# Revit family: Roof Decking-Side
name_source: partatom
category: Detail Items
revit_build: Autodesk Revit Architecture 2012 (Build: 20110210_1515)
units: mm (PartAtom-declared; Revit-internal decimal feet)

## types (26) — shared parameters

## per-type parameters (varying)
| type | Gauge | Height | Keynote | Rib Max | Rib Min | Width |
| 1 IR 20 | 20 | 0' - 1" | 05 31 00.C1 | 0' - 3" | 0' - 1" | 0' - 4" |
| 4.5 LS 16 | 16 | 0' - 4 1/2" | 05 31 00.C18 | 0' - 8" | 0' - 8" | 1' - 0" |
| 1.5 NR 18 | 18 | 0' - 1 1/2" | 05 31 00.C8 | 0' - 4 1/4" | 0' - 3 1/2" | 0' - 6" |
| 1.5 IR 18 | 18 | 0' - 1 1/2" | 05 31 00.C5 | 0' - 5 7/16" | 0' - 4 1/4" | 0' - 6" |
| 1.5 WR 18 | 18 | 0' - 1 1/2" | 05 31 00.C11 | 0' - 5 9/16" | 0' - 5" | 0' - 6" |
| 3 DR 16 | 16 | 0' - 3" | 05 31 00.C14 | 0' - 6" | 0' - 5 3/8" | 0' - 8" |
| 6 LS 16 | 16 | 0' - 6" | 05 31 00.C21 | 0' - 8" | 0' - 8" | 1' - 0" |
| 7.5 LS 16 | 16 | 0' - 7 1/2" | 05 31 00.C24 | 0' - 8" | 0' - 8" | 1' - 0" |
| 1 IR 22 | 22 | 0' - 1" | 05 31 00.C2 | 0' - 3" | 0' - 1" | 0' - 4" |
| 1 IR 24 | 24 | 0' - 1" | 05 31 00.C3 | 0' - 3" | 0' - 1" | 0' - 4" |
| 1 IR 26 | 26 | 0' - 1" | 05 31 00.C4 | 0' - 3" | 0' - 1" | 0' - 4" |
| 1.5 IR 20 | 20 | 0' - 1 1/2" | 05 31 00.C6 | 0' - 5 7/16" | 0' - 4 1/4" | 0' - 6" |
| 1.5 IR 22 | 22 | 0' - 1 1/2" | 05 31 00.C7 | 0' - 5 7/16" | 0' - 4 1/4" | 0' - 6" |
| 1.5 NR 20 | 20 | 0' - 1 1/2" | 05 31 00.C9 | 0' - 4 1/4" | 0' - 3 1/2" | 0' - 6" |
| 1.5 NR 22 | 22 | 0' - 1 1/2" | 05 31 00.C10 | 0' - 4 1/4" | 0' - 3 1/2" | 0' - 6" |
| 1.5 WR 20 | 20 | 0' - 1 1/2" | 05 31 00.C12 | 0' - 5 9/16" | 0' - 5" | 0' - 6" |
| 1.5 WR 22 | 22 | 0' - 1 1/2" | 05 31 00.C13 | 0' - 5 9/16" | 0' - 5" | 0' - 6" |
| 3 DR 18 | 18 | 0' - 3" | 05 31 00.C15 | 0' - 6" | 0' - 5 3/8" | 0' - 8" |
| 3 DR 20 | 20 | 0' - 3" | 05 31 00.C16 | 0' - 6" | 0' - 5 3/8" | 0' - 8" |
| 3 DR 22 | 22 | 0' - 3" | 05 31 00.C17 | 0' - 6" | 0' - 5 3/8" | 0' - 8" |
| 4.5 LS 18 | 18 | 0' - 4 1/2" | 05 31 00.C19 | 0' - 8" | 0' - 8" | 1' - 0" |
| 4.5 LS 20 | 20 | 0' - 4 1/2" | 05 31 00.C20 | 0' - 8" | 0' - 8" | 1' - 0" |
| 6 LS 18 | 18 | 0' - 6" | 05 31 00.C22 | 0' - 8" | 0' - 8" | 1' - 0" |
| 6 LS 20 | 20 | 0' - 6" | 05 31 00.C23 | 0' - 8" | 0' - 8" | 1' - 0" |
| 7.5 LS 18 | 18 | 0' - 7 1/2" | 05 31 00.C25 | 0' - 8" | 0' - 8" | 1' - 0" |
| 7.5 LS 20 | 20 | 0' - 7 1/2" | 05 31 00.C26 | 0' - 8" | 0' - 8" | 1' - 0" |

## geometry (parser evidence)
native form markers: Sweep x1
no freeform markers — native parametric forms only
